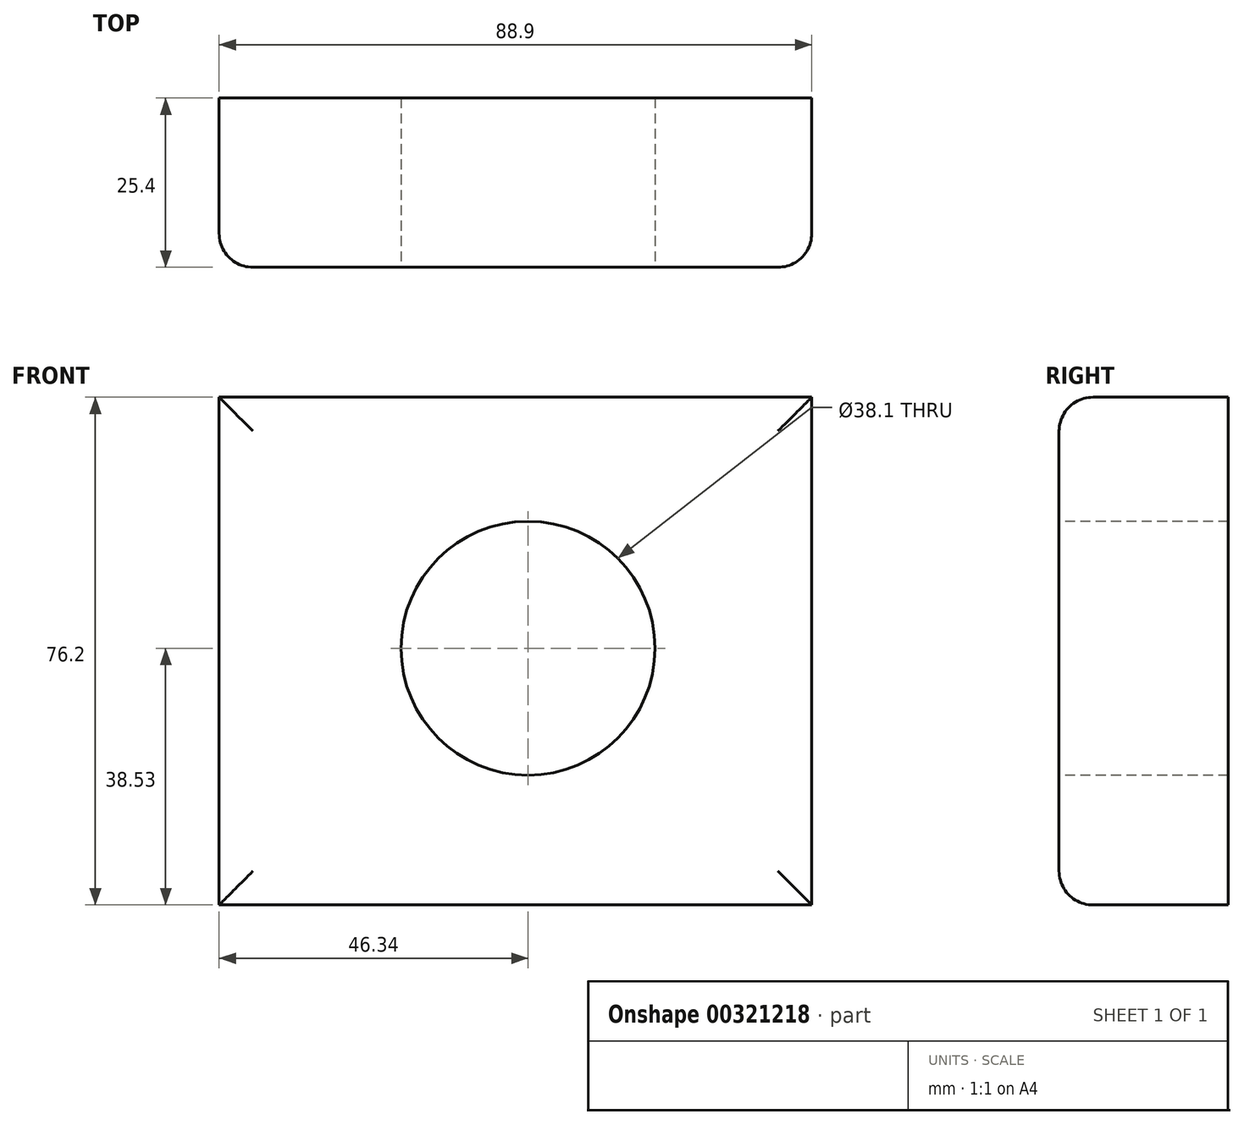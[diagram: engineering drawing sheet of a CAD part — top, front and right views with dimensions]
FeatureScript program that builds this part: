
annotation { "Feature Type Name" : "Feature", "Feature Type Description" : "" }
export const myFeature = defineFeature(function(context is Context, id is Id, definition is map)
    precondition{}
    {
        {
            var Q0;
            Q0=qCreatedBy(makeId("Front.planeOp"),FACE);
            var sketch = newSketch(context, id + "F0", { "sketchPlane" : qUnion([Q0])});
            skLineSegment(sketch, "E0.bottom", {"start": v(-46.34, 37.67) * mm, "end": v(42.56, 37.67) * mm});
            skLineSegment(sketch, "E0.top", {"start": v(-46.34, -38.53) * mm, "end": v(42.56, -38.53) * mm});
            skLineSegment(sketch, "E0.left", {"start": v(-46.34, 37.67) * mm, "end": v(-46.34, -38.53) * mm});
            skLineSegment(sketch, "E0.right", {"start": v(42.56, 37.67) * mm, "end": v(42.56, -38.53) * mm});
            skSolve(sketch);
        }
        {
            var Q0;
            Q0=makeQuery(id+"F0.imprint","IMPRINT",FACE,{"disambiguationData":[TD([[makeQuery(id+"F0.imprint","IMPRINT",EDGE,{"derivedFrom":sQuery(id+"F0.wireOp",EDGE,"E0.bottom")}),-1.0]])]});
            extrude(context, id + "F1", {"entities" : qUnion([Q0]), "depth" : 25.4 * mm});
        }
        {
            var Q0;
            Q0=makeQuery(id+"F1.opExtrude","CAP_FACE",FACE,{"disambiguationData":[OSD([sQuery(id+"F0.wireOp",EDGE,"E0.bottom"),sQuery(id+"F0.wireOp",EDGE,"E0.top"),sQuery(id+"F0.wireOp",EDGE,"E0.left"),sQuery(id+"F0.wireOp",EDGE,"E0.right")])],"isStart":false});
            var sketch = newSketch(context, id + "F2", { "sketchPlane" : qUnion([Q0])});
            skCircle(sketch, "E1", {"center": v(0, 0) * mm, "radius": 19.05 * mm});
            skSolve(sketch);
        }
        {
            var Q0;
            Q0=makeQuery(id+"F2.imprint","IMPRINT",FACE,{"disambiguationData":[TD([[makeQuery(id+"F2.imprint","IMPRINT",EDGE,{"derivedFrom":sQuery(id+"F2.wireOp",EDGE,"E1")}),1.0]])]});
            extrude(context, id + "F3", {"entities" : qUnion([Q0]), "operationType" : NewBodyOperationType.REMOVE, "oppositeDirection" : true, "depth" : 25.4 * mm});
        }
        {
            var Q0;
            Q0=makeQuery(id+"F1.opExtrude","CAP_EDGE",EDGE,{"disambiguationData":[OSD([sQuery(id+"F0.wireOp",EDGE,"E0.left")])],"isStart":false});
            var Q1;
            Q1=makeQuery(id+"F1.opExtrude","CAP_EDGE",EDGE,{"disambiguationData":[OSD([sQuery(id+"F0.wireOp",EDGE,"E0.bottom")])],"isStart":false});
            var Q2;
            Q2=makeQuery(id+"F1.opExtrude","CAP_EDGE",EDGE,{"disambiguationData":[OSD([sQuery(id+"F0.wireOp",EDGE,"E0.right")])],"isStart":false});
            var Q3;
            Q3=makeQuery(id+"F1.opExtrude","CAP_EDGE",EDGE,{"disambiguationData":[OSD([sQuery(id+"F0.wireOp",EDGE,"E0.top")])],"isStart":false});
            fillet(context, id + "F4", {"entities" : qUnion([Q0, Q1, Q2, Q3]), "radius" : 5.08 * mm, "tangentPropagation" : true, "allowEdgeOverflow" : false});
        }
    });
